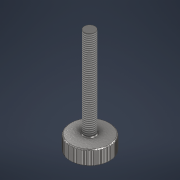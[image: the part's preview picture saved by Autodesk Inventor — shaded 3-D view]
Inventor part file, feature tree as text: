
AUTODESK INVENTOR PART (.ipt)
format: ipt  version: 2025 (Build 290162010, 162A)  size: 508,416 bytes
history: native  units: mm
features: extrude x3, sketch x3, chamfer x2, thread x1, pattern_circular x1
ambient origin geometry x8: Origin, YZ Plane, XZ Plane, XY Plane, X Axis, Y Axis, Z Axis, Center Point
bodies: Solid1 (feature_tree)
feature tree (10):
  extrude  "Extrusion1"  Depth=4.0mm TaperAngle=0.0deg
  extrude  "Extrusion2"  Depth=25.0mm TaperAngle=0.0deg
  chamfer  "Chamfer1"  Distance=0.25mm Angle=45.0deg
  thread  "Thread1"  [1 undecoded]
  sketch  "Sketch3"  dims[d11=0.25mm d12=0.05mm d13=0.25mm d14=2.0mm d15=45.0deg d16=0.0mm d17=0.0mm d18=500.0mm d19=360.0deg]
  chamfer  "Chamfer2"  Distance=0.05mm
  extrude  "Extrusion3"  Depth=0.05mm TaperAngle=45.0deg
  pattern_circular  "Circular Pattern1"  [2 undecoded]
  sketch  "Sketch1"  dims[d0=11.0mm d1=4.0mm d2=0.0mm]
  sketch  "Sketch2"  dims[d3=3.0mm d4=25.0mm d5=0.0mm d6=0.25mm d7=2.0mm d8=45.0deg d9=24.75mm d10=0.0mm]
note: 3 required parameter values undecoded (feature->parameter linkage not recoverable at this tier; creation-order binding heuristic only, values carry confidence <= 0.55)
